# Revit family: NBS_DudleyIndustriesLimited_TltPprBulkDpnsrs_PlasmaToiletRollDispenser
name_source: partatom
category: Furniture
revit_build: Autodesk Revit 2018 (Build: 20190510_1515(x64)
units: mm (PartAtom-declared; Revit-internal decimal feet)

## family parameters
Cut with Voids When Loaded = No
Host = Face
Room Calculation Point = No
Shared = No

## types (2) — shared parameters
AssetType = Fixed
Category = Pr_40_70_22_90:Toilet paper dispensers
Color = White
Default Elevation = 1050 mm
DispenserMaterial = NBS_DudleyIndustriesLimited_StainlessSteel_Brushed
DurationUnit = year
Finish = Brushed, polished, powder coated
IfcExportAs = IfcFurnitureType
IfcExportType = UNDEFINED
IsBuiltIn = Yes
ManufacturerName = Dudley Industries Limited
ManufacturerURL = www.dudleyindustries.com
Material = Stainless steel
MaterialsBody = Stainless steel
MaterialsFinishAndColour = Polished, brushed stainless steel, white powder coated
NBSCertification = www.nationalbimlibrary.com/cert/vy3ssiwh
NBSDescription = Toilet paper bulk dispensers
NBSReference = 45-35-72/366
NominalDepth = 129 mm  [stored 0.423228 ft]
NominalWidth = 126 mm  [stored 0.413386 ft]
Packing = 1 piece
ProductInformation = https://www.dudleyindustries.com
Shape = Rectangular
Status = UNSET
Style = Roll dispenser
Uniclass2015Code = Pr_40_70_22_90
Uniclass2015Title = Toilet paper dispensers
Uniclass2015Version = Products v1.18
Version = 1
WarrantyDescription = 10 Years
WarrantyDurationUnit = year
zero-valued in all types: NominalLength

## per-type parameters (varying)
| type | BIMObjectName | Description | Features | ModelNumber | Name | NominalHeight | Size | Weight |
| PlasmaToiletRollDispenser_2Roll | NBS_DudleyIndustriesLimited_ToiletPaperBulkDispensers_PlasmaToiletRollDispenser_2Roll | 2 roll toilet roll dispenser | Easy access for servicing, secure locking mechanism | 77972 PS/SS/WH | ToiletPaperBulkDispensers_PlasmaToiletRollDispenser_2Roll_DudleyIndustriesLimited | 330 mm | 129 x 330 x 126 mm | 1.8 kg |
| PlasmaToiletRollDispenser_3Roll | NBS_DudleyIndustriesLimited_ToiletPaperBulkDispensers_PlasmaToiletRollDispenser_3Roll | 3 roll toilet roll dispenser | Ensures spare rolls are always available, secure locking mechanism | 77974 PS/SS/WH | ToiletPaperBulkDispensers_PlasmaToiletRollDispenser_3Roll_DudleyIndustriesLimited | 405 mm | 129 x 405 x 126 mm | 1.9 kg |

note: column(s) folded — value = type name in every type: ModelReference

note: [stored X ft] marks values corroborated as IEEE doubles in the binary element streams (Revit-internal decimal feet)

## geometry (parser evidence)
native form markers: Sweep x2
no freeform markers — native parametric forms only
